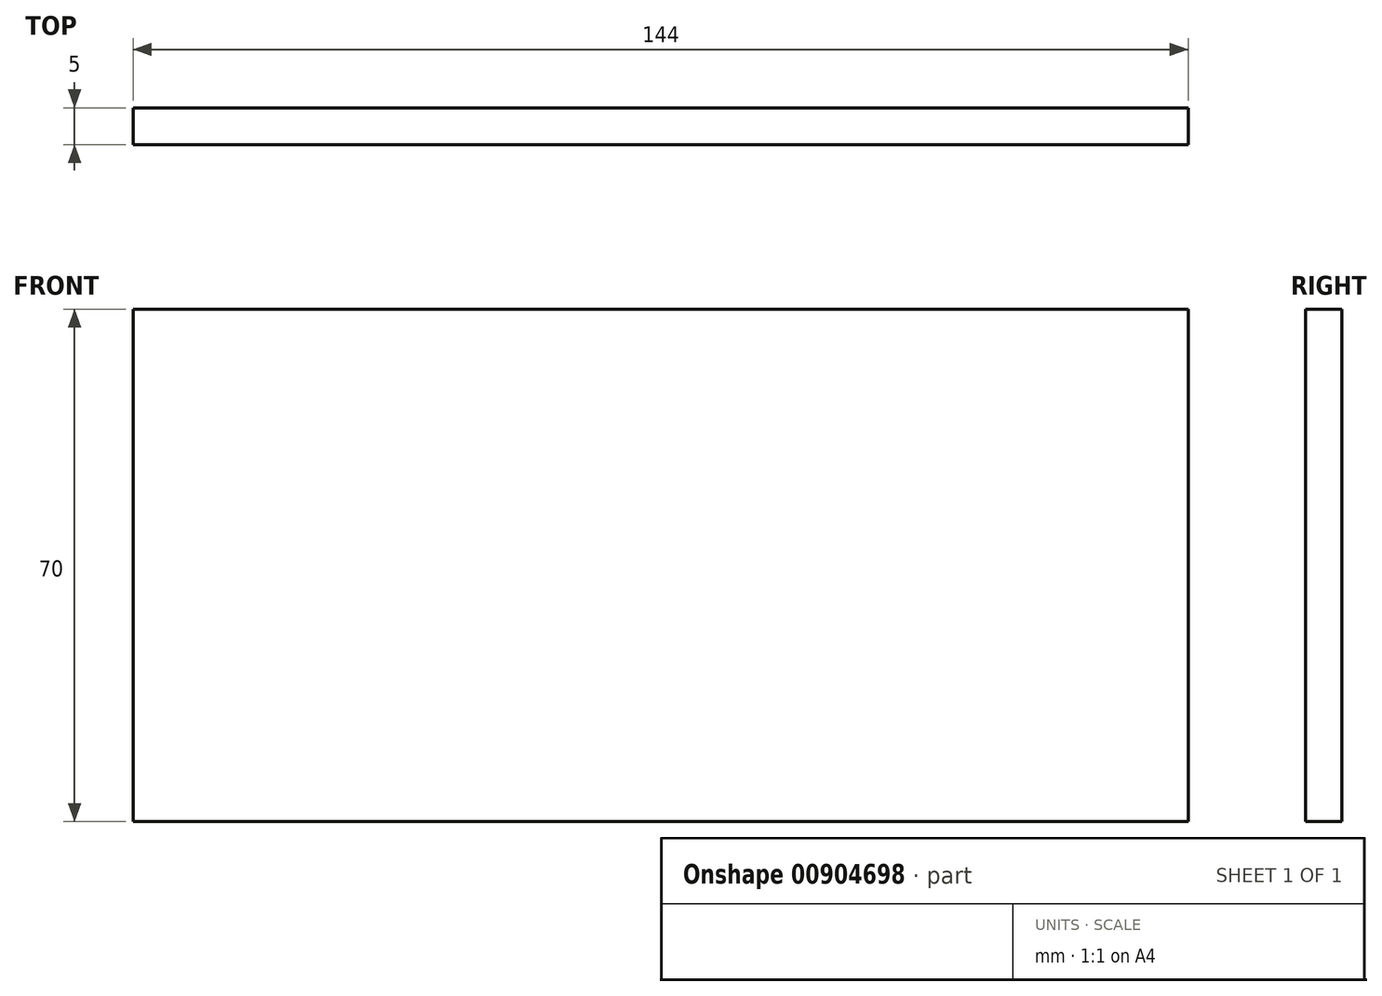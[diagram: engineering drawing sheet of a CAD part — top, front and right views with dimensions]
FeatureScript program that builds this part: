
annotation { "Feature Type Name" : "Feature", "Feature Type Description" : "" }
export const myFeature = defineFeature(function(context is Context, id is Id, definition is map)
    precondition{}
    {
        {
            var Q0;
            Q0=qCreatedBy(makeId("Front.planeOp"),FACE);
            var sketch = newSketch(context, id + "F0", { "sketchPlane" : qUnion([Q0])});
            skLineSegment(sketch, "E0.bottom", {"start": v(-86.38, 45.28) * mm, "end": v(57.62, 45.28) * mm});
            skLineSegment(sketch, "E0.top", {"start": v(-86.38, -24.72) * mm, "end": v(57.62, -24.72) * mm});
            skLineSegment(sketch, "E0.left", {"start": v(-86.38, 45.28) * mm, "end": v(-86.38, -24.72) * mm});
            skLineSegment(sketch, "E0.right", {"start": v(57.62, 45.28) * mm, "end": v(57.62, -24.72) * mm});
            skSolve(sketch);
        }
        {
            var Q0;
            Q0=makeQuery(id+"F0.imprint","IMPRINT",FACE,{"disambiguationData":[TD([[makeQuery(id+"F0.imprint","IMPRINT",EDGE,{"derivedFrom":sQuery(id+"F0.wireOp",EDGE,"E0.bottom")}),-1.0]])]});
            extrude(context, id + "F1", {"entities" : qUnion([Q0]), "depth" : 5 * mm, "offsetDistance" : 25 * mm});
        }
    });
